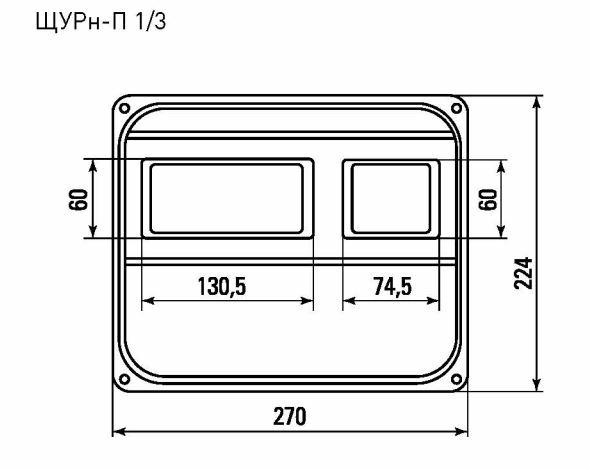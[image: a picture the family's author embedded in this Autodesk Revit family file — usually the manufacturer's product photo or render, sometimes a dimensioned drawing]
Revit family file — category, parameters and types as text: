
# Revit family: EKF_EE_ЦокольВСбореTrivia_AVERES
name_source: partatom
category: Электрооборудование
units: mm (PartAtom-declared; Revit-internal decimal feet)

## family parameters
Всегда вертикально = Нет
На основе рабочей плоскости = Да
Общий = Нет
При загрузке вырезать с полостями = Нет
Размер круглого соединителя = Использовать диаметр
Тип детали = Силовой щит
Точка расчета площади = Нет

## types (12) — shared parameters
ADSK_Материал = RAL 7035_Сталь
ADSK_Размер_Высота = 100 мм
Б400 = EKF_EE_БоковыеПанелиЦоколяTrivia_AVERES : Боковые панели цоколя Г400 EKF AVERES
Б600 = EKF_EE_БоковыеПанелиЦоколяTrivia_AVERES : Боковые панели цоколя Г600 EKF AVERES
Б800 = EKF_EE_БоковыеПанелиЦоколяTrivia_AVERES : Боковые панели цоколя Г800 EKF AVERES
ПЗ_300 = EKF_EE_ПередняяЗадняяПанелиЦоколяTrivia_AVERES : Передняя и задняя панели цоколя Ш300 EKF AVERES
ПЗ_400 = EKF_EE_ПередняяЗадняяПанелиЦоколяTrivia_AVERES : Передняя и задняя панели цоколя Ш400 EKF AVERES
ПЗ_600 = EKF_EE_ПередняяЗадняяПанелиЦоколяTrivia_AVERES : Передняя и задняя панели цоколя Ш600 EKF AVERES
ПЗ_800 = EKF_EE_ПередняяЗадняяПанелиЦоколяTrivia_AVERES : Передняя и задняя панели цоколя Ш800 EKF AVERES
zero-valued in all types: Отметка по умолчанию

## per-type parameters (varying)
| type | ADSK_Размер_Глубина | ADSK_Размер_Ширина | БоковыеПанелиЦоколя | Глубина | Передня-Задняя_Панели | Ширина |
| Цоколь в сборе Ш300 Г400 | 410 мм | 310 мм | EKF_EE_БоковыеПанелиЦоколяTrivia_AVERES : Боковые панели цоколя Г400 EKF AVERES | 410 мм | EKF_EE_ПередняяЗадняяПанелиЦоколяTrivia_AVERES : Передняя и задняя панели цоколя Ш300 EKF AVERES | 310 мм |
| Цоколь в сборе Ш300 Г600 | 610 мм | 310 мм | EKF_EE_БоковыеПанелиЦоколяTrivia_AVERES : Боковые панели цоколя Г600 EKF AVERES | 610 мм | EKF_EE_ПередняяЗадняяПанелиЦоколяTrivia_AVERES : Передняя и задняя панели цоколя Ш300 EKF AVERES | 310 мм |
| Цоколь в сборе Ш300 Г800 | 810 мм | 310 мм | EKF_EE_БоковыеПанелиЦоколяTrivia_AVERES : Боковые панели цоколя Г800 EKF AVERES | 810 мм | EKF_EE_ПередняяЗадняяПанелиЦоколяTrivia_AVERES : Передняя и задняя панели цоколя Ш300 EKF AVERES | 310 мм |
| Цоколь в сборе Ш400 Г400 | 410 мм | 410 мм | EKF_EE_БоковыеПанелиЦоколяTrivia_AVERES : Боковые панели цоколя Г400 EKF AVERES | 410 мм | EKF_EE_ПередняяЗадняяПанелиЦоколяTrivia_AVERES : Передняя и задняя панели цоколя Ш400 EKF AVERES | 410 мм |
| Цоколь в сборе Ш400 Г600 | 610 мм | 410 мм | EKF_EE_БоковыеПанелиЦоколяTrivia_AVERES : Боковые панели цоколя Г600 EKF AVERES | 610 мм | EKF_EE_ПередняяЗадняяПанелиЦоколяTrivia_AVERES : Передняя и задняя панели цоколя Ш400 EKF AVERES | 410 мм |
| Цоколь в сборе Ш400 Г800 | 810 мм | 410 мм | EKF_EE_БоковыеПанелиЦоколяTrivia_AVERES : Боковые панели цоколя Г800 EKF AVERES | 810 мм | EKF_EE_ПередняяЗадняяПанелиЦоколяTrivia_AVERES : Передняя и задняя панели цоколя Ш400 EKF AVERES | 410 мм |
| Цоколь в сборе Ш600 Г400 | 410 мм | 610 мм | EKF_EE_БоковыеПанелиЦоколяTrivia_AVERES : Боковые панели цоколя Г400 EKF AVERES | 410 мм | EKF_EE_ПередняяЗадняяПанелиЦоколяTrivia_AVERES : Передняя и задняя панели цоколя Ш600 EKF AVERES | 610 мм |
| Цоколь в сборе Ш600 Г600 | 610 мм | 610 мм | EKF_EE_БоковыеПанелиЦоколяTrivia_AVERES : Боковые панели цоколя Г600 EKF AVERES | 610 мм | EKF_EE_ПередняяЗадняяПанелиЦоколяTrivia_AVERES : Передняя и задняя панели цоколя Ш600 EKF AVERES | 610 мм |
| Цоколь в сборе Ш600 Г800 | 810 мм | 610 мм | EKF_EE_БоковыеПанелиЦоколяTrivia_AVERES : Боковые панели цоколя Г800 EKF AVERES | 810 мм | EKF_EE_ПередняяЗадняяПанелиЦоколяTrivia_AVERES : Передняя и задняя панели цоколя Ш600 EKF AVERES | 610 мм |
| Цоколь в сборе Ш800 Г400 | 410 мм | 810 мм | EKF_EE_БоковыеПанелиЦоколяTrivia_AVERES : Боковые панели цоколя Г400 EKF AVERES | 410 мм | EKF_EE_ПередняяЗадняяПанелиЦоколяTrivia_AVERES : Передняя и задняя панели цоколя Ш800 EKF AVERES | 810 мм |
| Цоколь в сборе Ш800 Г600 | 610 мм | 810 мм | EKF_EE_БоковыеПанелиЦоколяTrivia_AVERES : Боковые панели цоколя Г600 EKF AVERES | 610 мм | EKF_EE_ПередняяЗадняяПанелиЦоколяTrivia_AVERES : Передняя и задняя панели цоколя Ш800 EKF AVERES | 810 мм |
| Цоколь в сборе Ш800 Г800 | 810 мм | 810 мм | EKF_EE_БоковыеПанелиЦоколяTrivia_AVERES : Боковые панели цоколя Г800 EKF AVERES | 810 мм | EKF_EE_ПередняяЗадняяПанелиЦоколяTrivia_AVERES : Передняя и задняя панели цоколя Ш800 EKF AVERES | 810 мм |
